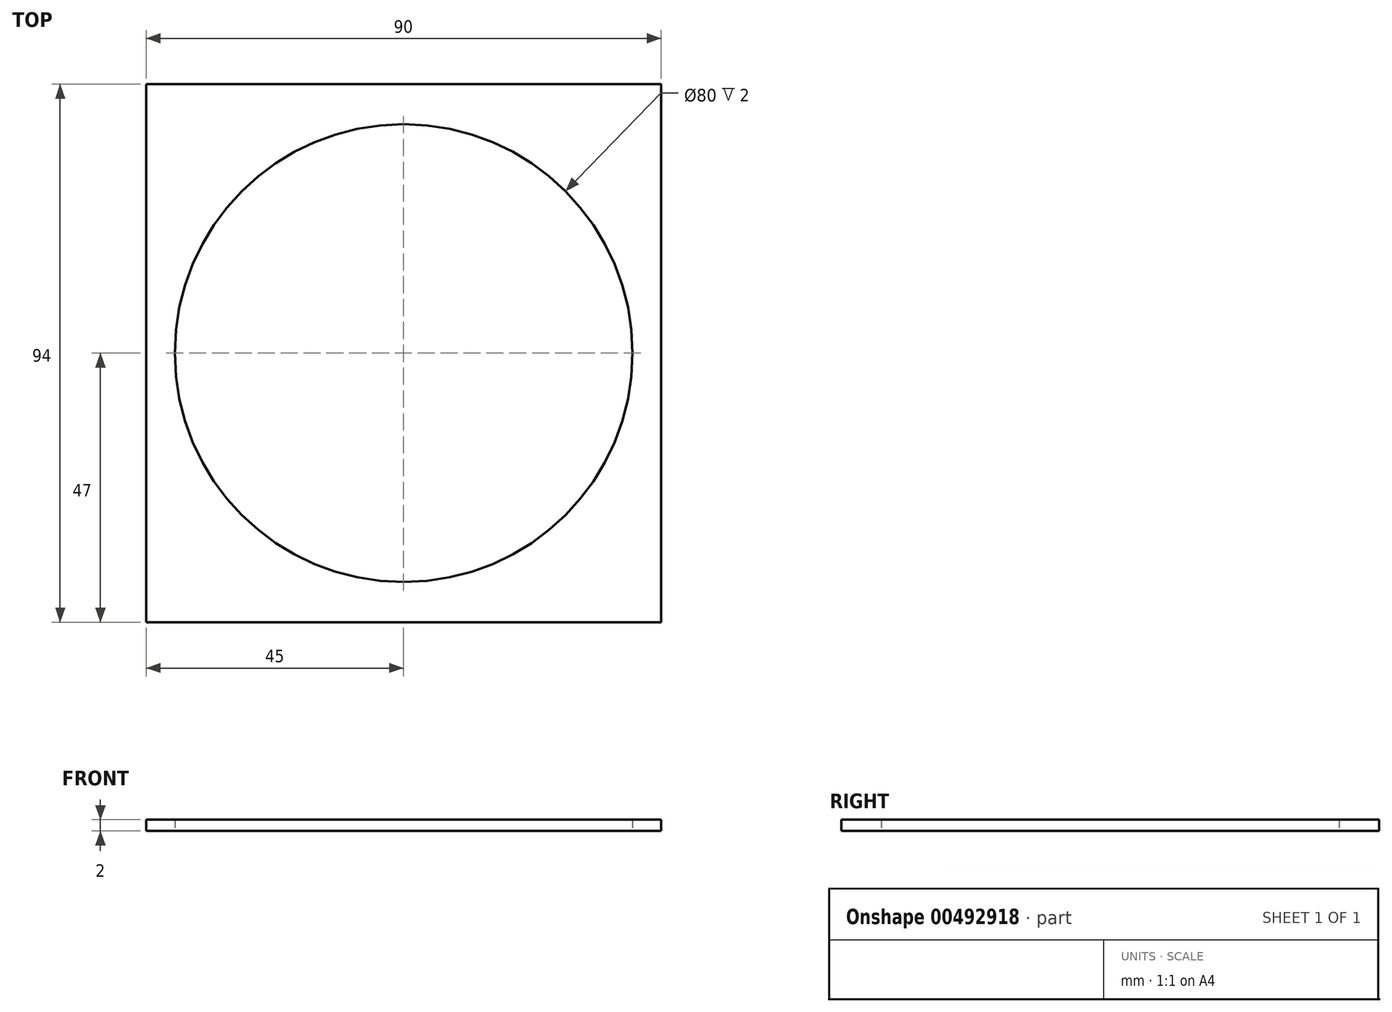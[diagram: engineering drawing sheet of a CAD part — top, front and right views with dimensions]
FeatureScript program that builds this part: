
annotation { "Feature Type Name" : "Feature", "Feature Type Description" : "" }
export const myFeature = defineFeature(function(context is Context, id is Id, definition is map)
    precondition{}
    {
        {
            var Q0;
            Q0=qCreatedBy(makeId("Top.planeOp"),FACE);
            var sketch = newSketch(context, id + "F0", { "sketchPlane" : qUnion([Q0])});
            skLineSegment(sketch, "E0.bottom", {"start": v(45, 47) * mm, "end": v(-45, 47) * mm});
            skLineSegment(sketch, "E0.top", {"start": v(45, -47) * mm, "end": v(-45, -47) * mm});
            skLineSegment(sketch, "E0.left", {"start": v(45, 47) * mm, "end": v(45, -47) * mm});
            skLineSegment(sketch, "E0.right", {"start": v(-45, 47) * mm, "end": v(-45, -47) * mm});
            skPoint(sketch, "E0.middle", {"position": v(0, 0) * mm});
            skCircle(sketch, "E1", {"center": v(0, 0) * mm, "radius": 40 * mm});
            skSolve(sketch);
        }
        {
            var Q0;
            Q0=makeQuery(id+"F0.imprint","IMPRINT",FACE,{"disambiguationData":[TD([[makeQuery(id+"F0.imprint","IMPRINT",EDGE,{"derivedFrom":sQuery(id+"F0.wireOp",EDGE,"E0.bottom")}),1.0]])]});
            extrude(context, id + "F1", {"entities" : qUnion([Q0]), "depth" : 2 * mm, "offsetDistance" : 25 * mm});
        }
    });
